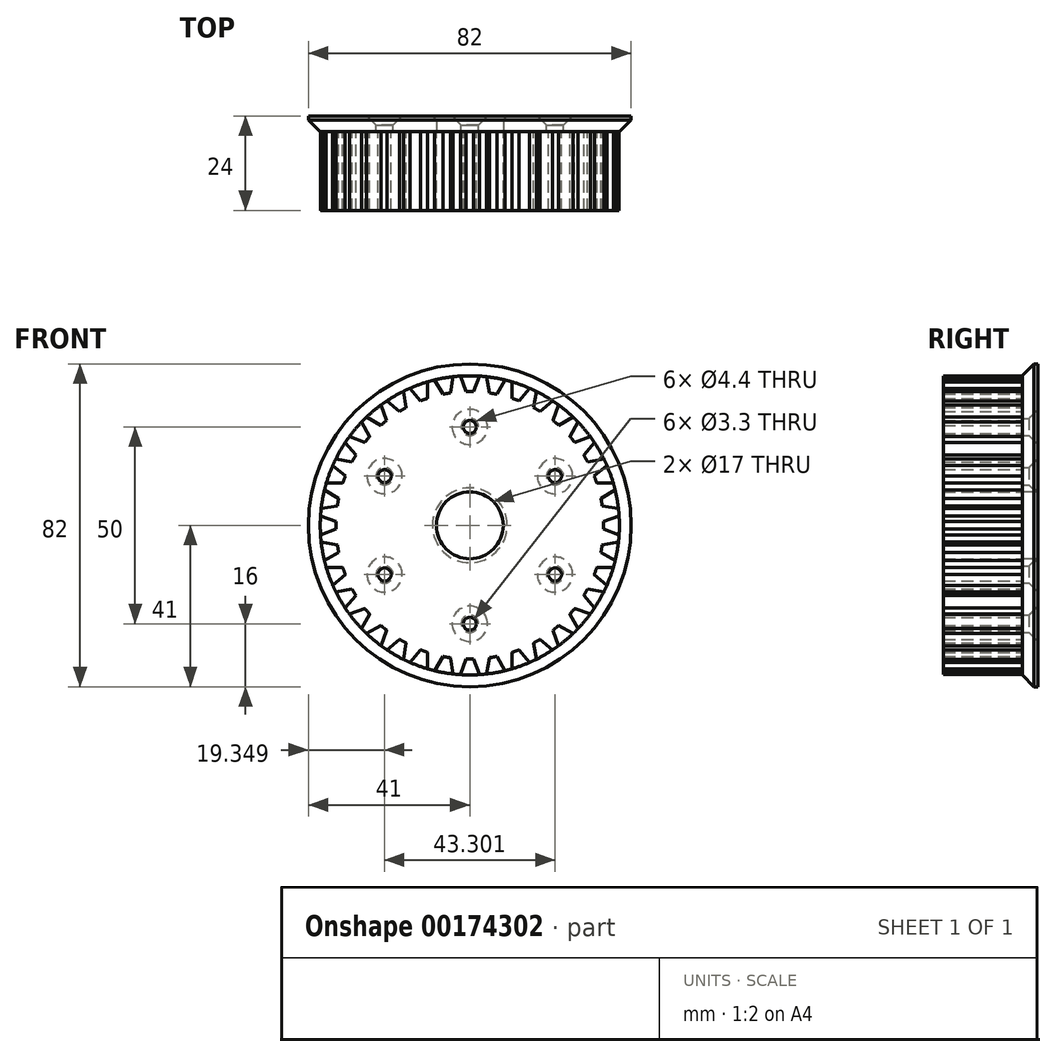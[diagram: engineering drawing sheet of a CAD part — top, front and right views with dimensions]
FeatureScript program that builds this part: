
annotation { "Feature Type Name" : "Feature", "Feature Type Description" : "" }
export const myFeature = defineFeature(function(context is Context, id is Id, definition is map)
    precondition{}
    {
        {
            var Q0;
            Q0=qCreatedBy(makeId("Front.planeOp"),FACE);
            var sketch = newSketch(context, id + "F0", { "sketchPlane" : qUnion([Q0])});
            skCircle(sketch, "E0", {"center": v(0, 0) * mm, "radius": 38 * mm});
            skArc(sketch, "E1", {"start": v(0.97, 33.99) * mm, "mid": v(0, 34) * mm, "end": v(-0.97, 33.99) * mm});
            skCircle(sketch, "E2", {"center": v(0, 0) * mm, "radius": 8.5 * mm});
            skLineSegment(sketch, "E3", {"start": v(0, 8.5) * mm, "end": v(0, 38) * mm, "construction": true});
            skLineSegment(sketch, "E4", {"start": v(0.97, 33.99) * mm, "end": v(2.4, 37.92) * mm});
            skLineSegment(sketch, "E5.MirrorCS", {"start": v(-0.97, 33.99) * mm, "end": v(-2.4, 37.92) * mm});
            skSolve(sketch);
        }
        {
            var Q0;
            Q0 = qSketchRegion(id + "F0", true);
            extrude(context, id + "F1", {"entities" : qUnion([Q0]), "depth" : 20 * mm});
        }
        {
            var Q0;
            Q0=makeQuery(id+"F0.imprint","IMPRINT",FACE,{"disambiguationData":[TD([[makeQuery(id+"F0.imprint","IMPRINT",EDGE,{"derivedFrom":sQuery(id+"F0.wireOp",EDGE,"E1")}),-1.0]])]});
            extrude(context, id + "F2", {"entities" : qUnion([Q0]), "operationType" : NewBodyOperationType.REMOVE, "depth" : 20 * mm});
        }
        {
            var Q0;
            Q0=makeQuery(id+"F2.boolean.opBoolean","COPY",FACE,{"derivedFrom":makeQuery(id+"F2.opExtrude","SWEPT_FACE",FACE,{"disambiguationData":[OSD([sQuery(id+"F0.wireOp",EDGE,"E5.MirrorCS")])]})});
            var Q1;
            Q1=makeQuery(id+"F2.boolean.opBoolean","COPY",FACE,{"derivedFrom":makeQuery(id+"F2.opExtrude","SWEPT_FACE",FACE,{"disambiguationData":[OSD([sQuery(id+"F0.wireOp",EDGE,"E1")])]})});
            var Q2;
            Q2=makeQuery(id+"F2.boolean.opBoolean","COPY",FACE,{"derivedFrom":makeQuery(id+"F2.opExtrude","SWEPT_FACE",FACE,{"disambiguationData":[OSD([sQuery(id+"F0.wireOp",EDGE,"E4")])]})});
            var Q3;
            Q3=makeQuery(id+"F1.opExtrude","CAP_EDGE",EDGE,{"disambiguationData":[OSD([sQuery(id+"F0.wireOp",EDGE,"E2")])],"isStart":false});
            circularPattern(context, id + "F3", {"patternType" : PatternType.FACE, "operationType" : NewBodyOperationType.REMOVE, "faces" : qUnion([Q0, Q1, Q2]), "axis" : qUnion([Q3]), "angle" : 360 * degree, "instanceCount" : 36, "equalSpace" : true});
        }
        {
            var Q0;
            Q0=makeQuery(id+"F1.opExtrude","CAP_FACE",FACE,{"disambiguationData":[OSD([sQuery(id+"F0.wireOp",EDGE,"E0"),sQuery(id+"F0.wireOp",EDGE,"E2")])],"isStart":true});
            var sketch = newSketch(context, id + "F4", { "sketchPlane" : qUnion([Q0])});
            skCircle(sketch, "E6", {"center": v(0, 0) * mm, "radius": 8.5 * mm});
            skCircle(sketch, "E7", {"center": v(0, 0) * mm, "radius": 41 * mm});
            skSolve(sketch);
        }
        {
            var Q0;
            Q0 = qSketchRegion(id + "F4", true);
            extrude(context, id + "F5", {"entities" : qUnion([Q0]), "depth" : 4 * mm});
        }
        {
            var Q0;
            Q0=makeQuery(id+"F5.opExtrude","CAP_EDGE",EDGE,{"disambiguationData":[OSD([sQuery(id+"F4.wireOp",EDGE,"E7")])],"isStart":true});
            chamfer(context, id + "F6", {"entities" : qUnion([Q0]), "width" : 3 * mm, "tangentPropagation" : true});
        }
        {
            var Q0;
            Q0=makeQuery(id+"F5.opExtrude","CAP_FACE",FACE,{"disambiguationData":[OSD([sQuery(id+"F4.wireOp",EDGE,"E6"),sQuery(id+"F4.wireOp",EDGE,"E7")])],"isStart":false});
            var sketch = newSketch(context, id + "F7", { "sketchPlane" : qUnion([Q0])});
            skPoint(sketch, "E8", {"position": v(0, 25) * mm});
            skPoint(sketch, "E9.1.0", {"position": v(-21.65, 12.5) * mm});
            skPoint(sketch, "E9.2.0", {"position": v(-21.65, -12.5) * mm});
            skPoint(sketch, "E9.center", {"position": v(0, 0) * mm});
            skPoint(sketch, "E10.0.3.0", {"position": v(0, -25) * mm});
            skPoint(sketch, "E11.0.4.0", {"position": v(21.65, -12.5) * mm});
            skPoint(sketch, "E11.0.5.0", {"position": v(21.65, 12.5) * mm});
            skSolve(sketch);
        }
        {
            var Q0;
            Q0=sQuery(id+"F7.wireOp",VERTEX,"E8");
            var Q1;
            Q1=sQuery(id+"F7.wireOp",VERTEX,"E11.0.5.0");
            var Q2;
            Q2=sQuery(id+"F7.wireOp",VERTEX,"E11.0.4.0");
            var Q3;
            Q3=sQuery(id+"F7.wireOp",VERTEX,"E10.0.3.0");
            var Q4;
            Q4=sQuery(id+"F7.wireOp",VERTEX,"E9.2.0");
            var Q5;
            Q5=sQuery(id+"F7.wireOp",VERTEX,"E9.1.0");
            var Q6;
            Q6=makeQuery(id+"F1.opExtrude","SWEPT_BODY",BODY,{"disambiguationData":[OSD([sQuery(id+"F0.wireOp",EDGE,"E0"),sQuery(id+"F0.wireOp",EDGE,"E2")])]});
            var Q7;
            Q7=makeQuery(id+"F5.opExtrude","SWEPT_BODY",BODY,{"disambiguationData":[OSD([sQuery(id+"F4.wireOp",EDGE,"E6"),sQuery(id+"F4.wireOp",EDGE,"E7")])]});
            hole(context, id + "F8", {"style" : HoleStyle.C_SINK, "endStyle" : HoleEndStyle.BLIND_IN_LAST, "standardTappedOrClearance" : lookupTablePath({ "fit" : "Normal", "standard" : "ISO", "engagement" : "75%", "pitch" : "0.7 mm", "size" : "M4", "type" : "Clearance & tapped" }), "standardBlindInLast" : lookupTablePath({ "standard" : "ISO", "fit" : "Standard", "engagement" : "75%", "pitch" : "0.7 mm", "size" : "M4", "type" : "Clearance & tapped" }), "holeDiameter" : 4.4 * mm, "cSinkDiameter" : 8.96 * mm, "cSinkAngle" : 90 * degree, "tapDrillDiameter" : 3.3 * mm, "showTappedDepth" : true, "holeDepth" : 21.1 * mm, "tappedDepth" : 19 * mm, "tapClearance" : 3, "startFromSketch" : true, "locations" : qUnion([Q0, Q1, Q2, Q3, Q4, Q5]), "scope" : qUnion([Q6, Q7]), "majorDiameter" : 4 * mm});
        }
        {
            var Q0;
            Q0=makeQuery(id+"F5.opExtrude","CAP_EDGE",EDGE,{"disambiguationData":[OSD([sQuery(id+"F4.wireOp",EDGE,"E6")])],"isStart":false});
            chamfer(context, id + "F9", {"entities" : qUnion([Q0]), "width" : 1 * mm, "tangentPropagation" : true});
        }
    });
